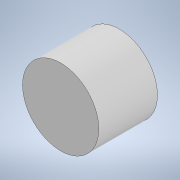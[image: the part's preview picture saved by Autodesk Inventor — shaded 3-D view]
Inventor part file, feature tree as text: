
AUTODESK INVENTOR PART (.ipt)
format: ipt  version: 2022 (Build 260153000, 153)  size: 100,864 bytes
history: native  units: in
note: dims shown in document units (in); Inventor stores cm internally (conversion verified against a paired STEP export)
features: extrude x1, sketch x1
ambient origin geometry x8: Origin, YZ Plane, XZ Plane, XY Plane, X Axis, Y Axis, Z Axis, Center Point
bodies: Body1 (feature_tree)
feature tree (2):
  extrude  "Extrusion1"  Depth=0.1969in
  sketch  "Sketch2"  dims[d1=0.2559in d2=0.2559in d3=0.1969in d4=0.0in]
